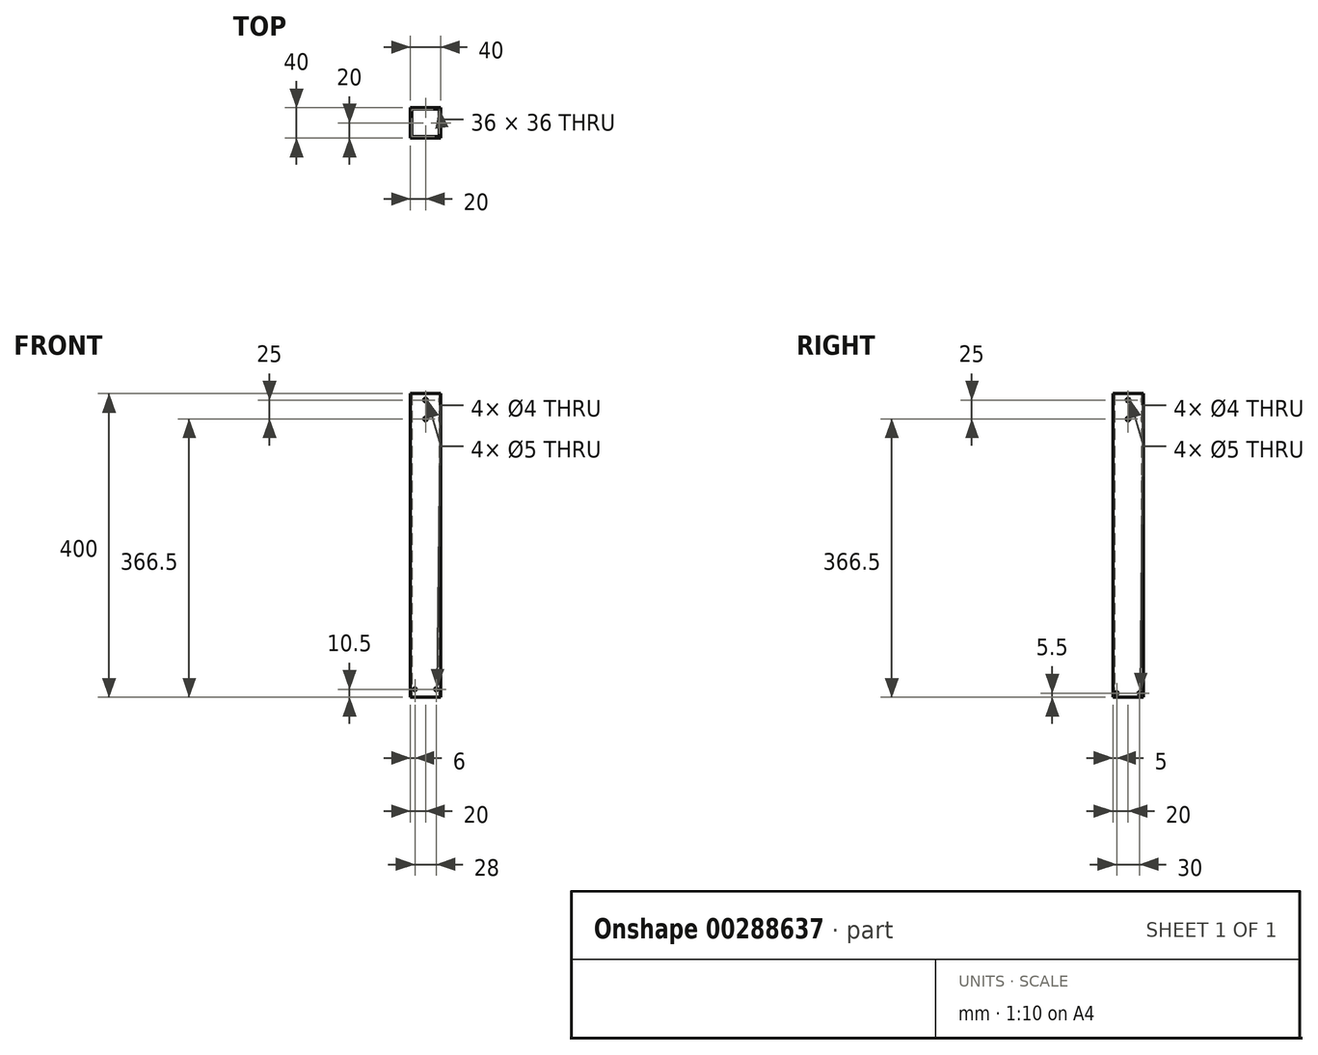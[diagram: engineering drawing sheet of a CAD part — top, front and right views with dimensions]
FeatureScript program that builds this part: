
annotation { "Feature Type Name" : "Feature", "Feature Type Description" : "" }
export const myFeature = defineFeature(function(context is Context, id is Id, definition is map)
    precondition{}
    {
        {
            var Q0;
            Q0=qCreatedBy(makeId("Top.planeOp"),FACE);
            var sketch = newSketch(context, id + "F0", { "sketchPlane" : qUnion([Q0])});
            skLineSegment(sketch, "E0.bottom", {"start": v(18, 18) * mm, "end": v(-18, 18) * mm});
            skLineSegment(sketch, "E0.top", {"start": v(18, -18) * mm, "end": v(-18, -18) * mm});
            skLineSegment(sketch, "E0.left", {"start": v(18, 18) * mm, "end": v(18, -18) * mm});
            skLineSegment(sketch, "E0.right", {"start": v(-18, 18) * mm, "end": v(-18, -18) * mm});
            skPoint(sketch, "E0.middle", {"position": v(0, 0) * mm});
            skLineSegment(sketch, "E1.bottom", {"start": v(20, 20) * mm, "end": v(-20, 20) * mm});
            skLineSegment(sketch, "E1.top", {"start": v(20, -20) * mm, "end": v(-20, -20) * mm});
            skLineSegment(sketch, "E1.left", {"start": v(20, 20) * mm, "end": v(20, -20) * mm});
            skLineSegment(sketch, "E1.right", {"start": v(-20, 20) * mm, "end": v(-20, -20) * mm});
            skSolve(sketch);
        }
        {
            var Q0;
            Q0=makeQuery(id+"F0.imprint","IMPRINT",FACE,{"disambiguationData":[TD([[makeQuery(id+"F0.imprint","IMPRINT",EDGE,{"derivedFrom":sQuery(id+"F0.wireOp",EDGE,"E0.bottom")}),-1.0]])]});
            extrude(context, id + "F1", {"entities" : qUnion([Q0]), "depth" : 400 * mm});
        }
        {
            var Q0;
            Q0=makeQuery(id+"F1.opExtrude","SWEPT_FACE",FACE,{"disambiguationData":[OSD([sQuery(id+"F0.wireOp",EDGE,"E1.left")])]});
            var sketch = newSketch(context, id + "F2", { "sketchPlane" : qUnion([Q0])});
            skCircle(sketch, "E2", {"center": v(-15, 5.5) * mm, "radius": 2 * mm});
            skCircle(sketch, "E3", {"center": v(15, 5.5) * mm, "radius": 2 * mm});
            skSolve(sketch);
        }
        {
            var Q0;
            Q0=makeQuery(id+"F2.imprint","IMPRINT",FACE,{"disambiguationData":[TD([[makeQuery(id+"F2.imprint","IMPRINT",EDGE,{"derivedFrom":sQuery(id+"F2.wireOp",EDGE,"E2")}),1.0]])]});
            var Q1;
            Q1=makeQuery(id+"F2.imprint","IMPRINT",FACE,{"disambiguationData":[TD([[makeQuery(id+"F2.imprint","IMPRINT",EDGE,{"derivedFrom":sQuery(id+"F2.wireOp",EDGE,"E3")}),1.0]])]});
            extrude(context, id + "F3", {"entities" : qUnion([Q0, Q1]), "operationType" : NewBodyOperationType.REMOVE, "oppositeDirection" : true, "depth" : 40 * mm, "offsetDistance" : 25 * mm});
        }
        {
            var Q0;
            Q0=makeQuery(id+"F1.opExtrude","SWEPT_FACE",FACE,{"disambiguationData":[OSD([sQuery(id+"F0.wireOp",EDGE,"E1.top")])]});
            var sketch = newSketch(context, id + "F4", { "sketchPlane" : qUnion([Q0])});
            skCircle(sketch, "E4", {"center": v(14, 10.5) * mm, "radius": 2 * mm});
            skCircle(sketch, "E5", {"center": v(-14, 10.5) * mm, "radius": 2 * mm});
            skSolve(sketch);
        }
        {
            var Q0;
            Q0=makeQuery(id+"F4.imprint","IMPRINT",FACE,{"disambiguationData":[TD([[makeQuery(id+"F4.imprint","IMPRINT",EDGE,{"derivedFrom":sQuery(id+"F4.wireOp",EDGE,"E5")}),1.0]])]});
            var Q1;
            Q1=makeQuery(id+"F4.imprint","IMPRINT",FACE,{"disambiguationData":[TD([[makeQuery(id+"F4.imprint","IMPRINT",EDGE,{"derivedFrom":sQuery(id+"F4.wireOp",EDGE,"E4")}),1.0]])]});
            extrude(context, id + "F5", {"entities" : qUnion([Q0, Q1]), "operationType" : NewBodyOperationType.REMOVE, "oppositeDirection" : true, "depth" : 40 * mm, "offsetDistance" : 25 * mm});
        }
        {
            var Q0;
            Q0=makeQuery(id+"F1.opExtrude","SWEPT_FACE",FACE,{"disambiguationData":[OSD([sQuery(id+"F0.wireOp",EDGE,"E1.left")])]});
            var sketch = newSketch(context, id + "F6", { "sketchPlane" : qUnion([Q0])});
            skCircle(sketch, "E6", {"center": v(0, 391.5) * mm, "radius": 2.5 * mm});
            skPoint(sketch, "E6.centerSnap0", {"position": v(0, 400) * mm});
            skCircle(sketch, "E7", {"center": v(0, 366.5) * mm, "radius": 2.5 * mm});
            skSolve(sketch);
        }
        {
            var Q0;
            Q0=makeQuery(id+"F6.imprint","IMPRINT",FACE,{"disambiguationData":[TD([[makeQuery(id+"F6.imprint","IMPRINT",EDGE,{"derivedFrom":sQuery(id+"F6.wireOp",EDGE,"E6")}),1.0]])]});
            var Q1;
            Q1=makeQuery(id+"F6.imprint","IMPRINT",FACE,{"disambiguationData":[TD([[makeQuery(id+"F6.imprint","IMPRINT",EDGE,{"derivedFrom":sQuery(id+"F6.wireOp",EDGE,"E7")}),1.0]])]});
            extrude(context, id + "F7", {"entities" : qUnion([Q0, Q1]), "operationType" : NewBodyOperationType.REMOVE, "oppositeDirection" : true, "depth" : 40 * mm, "offsetDistance" : 25 * mm});
        }
        {
            var Q0;
            Q0=makeQuery(id+"F1.opExtrude","SWEPT_FACE",FACE,{"disambiguationData":[OSD([sQuery(id+"F0.wireOp",EDGE,"E1.top")])]});
            var sketch = newSketch(context, id + "F8", { "sketchPlane" : qUnion([Q0])});
            skCircle(sketch, "E8", {"center": v(0, 391.5) * mm, "radius": 2.5 * mm});
            skPoint(sketch, "E8.centerSnap0", {"position": v(0, 400) * mm});
            skCircle(sketch, "E9", {"center": v(0, 366.5) * mm, "radius": 2.5 * mm});
            skSolve(sketch);
        }
        {
            var Q0;
            Q0=makeQuery(id+"F8.imprint","IMPRINT",FACE,{"disambiguationData":[TD([[makeQuery(id+"F8.imprint","IMPRINT",EDGE,{"derivedFrom":sQuery(id+"F8.wireOp",EDGE,"E8")}),1.0]])]});
            var Q1;
            Q1=makeQuery(id+"F8.imprint","IMPRINT",FACE,{"disambiguationData":[TD([[makeQuery(id+"F8.imprint","IMPRINT",EDGE,{"derivedFrom":sQuery(id+"F8.wireOp",EDGE,"E9")}),1.0]])]});
            extrude(context, id + "F9", {"entities" : qUnion([Q0, Q1]), "operationType" : NewBodyOperationType.REMOVE, "oppositeDirection" : true, "depth" : 40 * mm, "offsetDistance" : 25 * mm});
        }
    });
